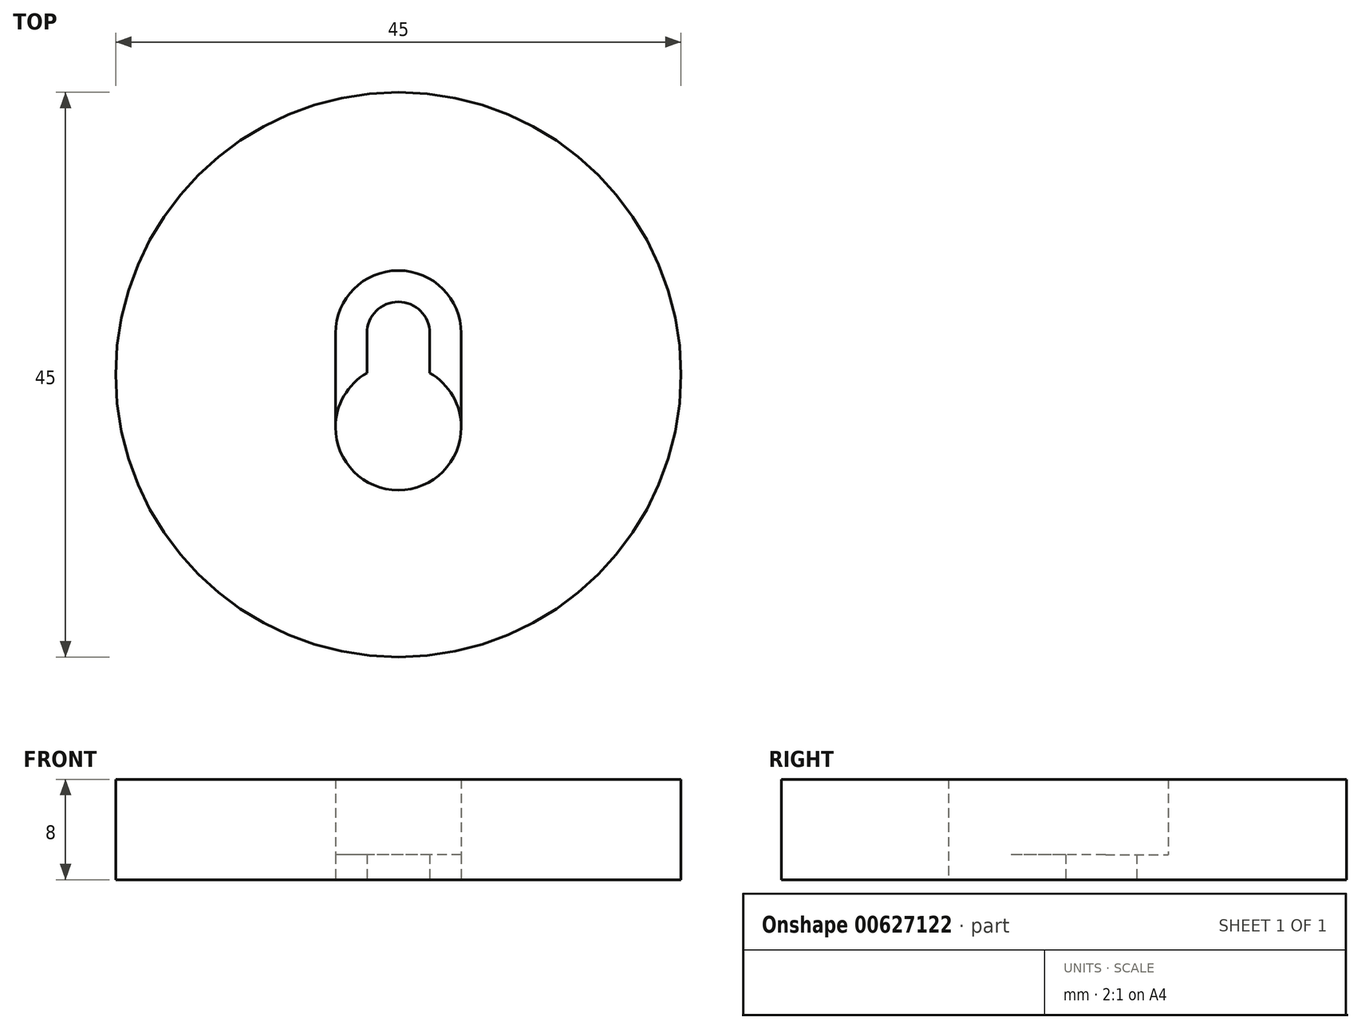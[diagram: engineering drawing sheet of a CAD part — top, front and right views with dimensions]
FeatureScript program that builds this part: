
annotation { "Feature Type Name" : "Feature", "Feature Type Description" : "" }
export const myFeature = defineFeature(function(context is Context, id is Id, definition is map)
    precondition{}
    {
        {
            var Q0;
            Q0=qCreatedBy(makeId("Top.planeOp"),FACE);
            var sketch = newSketch(context, id + "F0", { "sketchPlane" : qUnion([Q0])});
            skCircle(sketch, "E0", {"center": v(0, 0) * mm, "radius": 22.5 * mm});
            skCircle(sketch, "E1", {"center": v(0, 3.3) * mm, "radius": 2.5 * mm});
            skCircle(sketch, "E2", {"center": v(0, -4.2) * mm, "radius": 5 * mm});
            skLineSegment(sketch, "E3", {"start": v(-2.5, 3.3) * mm, "end": v(-2.5, 0.13) * mm});
            skLineSegment(sketch, "E4", {"start": v(2.5, 3.3) * mm, "end": v(2.5, 0.13) * mm});
            skLineSegment(sketch, "E5", {"start": v(-5, -4.2) * mm, "end": v(-5, 3.3) * mm});
            skLineSegment(sketch, "E6", {"start": v(5, -4.2) * mm, "end": v(5, 3.3) * mm});
            skCircle(sketch, "E7", {"center": v(0, 3.3) * mm, "radius": 5 * mm});
            skSolve(sketch);
        }
        {
            var Q0;
            Q0=makeQuery(id+"F0.imprint","IMPRINT",FACE,{"disambiguationData":[TD([[makeQuery(id+"F0.imprint","IMPRINT",EDGE,{"derivedFrom":sQuery(id+"F0.wireOp",EDGE,"E0")}),1.0]])]});
            var Q1;
            {var subQ0=sQuery(id+"F0.wireOp",EDGE,"E5");Q1=makeQuery(id+"F0.imprint","IMPRINT",FACE,{"disambiguationData":[TD([[makeQuery(id+"F0.imprint","IMPRINT",EDGE,{"derivedFrom":subQ0}),-1.0]])]});}
            var Q2;
            {var subQ0=sQuery(id+"F0.wireOp",EDGE,"E3");Q2=makeQuery(id+"F0.imprint","IMPRINT",FACE,{"disambiguationData":[TD([[makeQuery(id+"F0.imprint","IMPRINT",EDGE,{"derivedFrom":subQ0}),-1.0]])]});}
            var Q3;
            {var subQ0=sQuery(id+"F0.wireOp",EDGE,"E6");Q3=makeQuery(id+"F0.imprint","IMPRINT",FACE,{"disambiguationData":[TD([[makeQuery(id+"F0.imprint","IMPRINT",EDGE,{"derivedFrom":subQ0}),1.0]])]});}
            extrude(context, id + "F1", {"entities" : qUnion([Q0, Q1, Q2, Q3]), "depth" : 2 * mm, "offsetDistance" : 25 * mm});
        }
        {
            var Q0;
            Q0=makeQuery(id+"F0.imprint","IMPRINT",FACE,{"disambiguationData":[TD([[makeQuery(id+"F0.imprint","IMPRINT",EDGE,{"derivedFrom":sQuery(id+"F0.wireOp",EDGE,"E0")}),1.0]])]});
            extrude(context, id + "F2", {"entities" : qUnion([Q0]), "operationType" : NewBodyOperationType.ADD, "depth" : 8 * mm, "offsetDistance" : 25 * mm});
        }
    });
